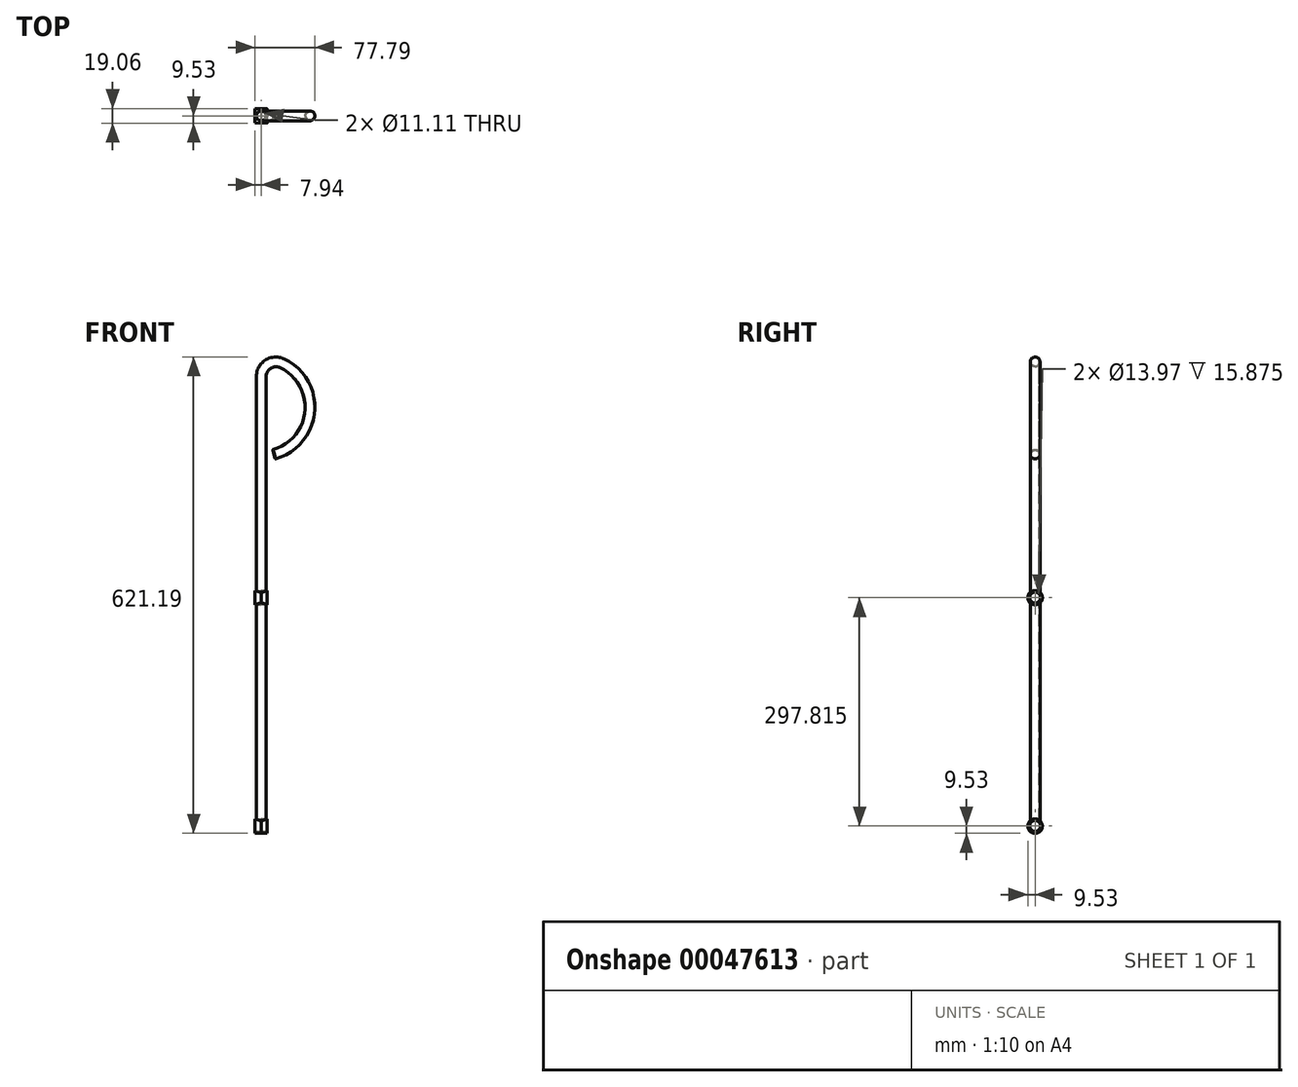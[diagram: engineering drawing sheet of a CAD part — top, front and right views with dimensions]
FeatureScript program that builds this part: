
annotation { "Feature Type Name" : "Feature", "Feature Type Description" : "" }
export const myFeature = defineFeature(function(context is Context, id is Id, definition is map)
    precondition{}
    {
        {
            var Q0;
            Q0=qCreatedBy(makeId("Front.planeOp"),FACE);
            var sketch = newSketch(context, id + "F0", { "sketchPlane" : qUnion([Q0])});
            skLineSegment(sketch, "E0", {"start": v(0, 0) * mm, "end": v(0, 586.26) * mm});
            skArc(sketch, "E1", {"start": v(16.44, 484.76) * mm, "mid": v(63.24, 540.36) * mm, "end": v(27.21, 603.47) * mm});
            skLineSegment(sketch, "E2", {"start": v(0, 546.1) * mm, "end": v(30.83, 431.05) * mm, "construction": true});
            skPoint(sketch, "E3.visualSharp", {"position": v(0, 609.6) * mm});
            skArc(sketch, "E3.filletArc", {"start": v(27.21, 603.47) * mm, "mid": v(8.87, 602.36) * mm, "end": v(0, 586.26) * mm});
            skSolve(sketch);
        }
        {
            var Q0;
            Q0=qCreatedBy(makeId("Top.planeOp"),FACE);
            var sketch = newSketch(context, id + "F1", { "sketchPlane" : qUnion([Q0])});
            skCircle(sketch, "E4", {"center": v(0, 0) * mm, "radius": 6.35 * mm});
            skCircle(sketch, "E5", {"center": v(0, 0) * mm, "radius": 5.56 * mm});
            skSolve(sketch);
        }
        {
            var Q0;
            Q0=qSketchRegion(id+"F1",true);
            var Q1;
            Q1=qConstructionFilter(qBodyType(qCreatedBy(id+"F0",EDGE),BodyType.WIRE),ConstructionObject.NO);
            sweep(context, id + "F2", {"profiles" : qUnion([Q0]), "path" : qUnion([Q1])});
        }
        {
            var Q0;
            Q0=makeQuery(id+"F2.opSweep","CAP_EDGE",EDGE,{"disambiguationData":[OSD([sQuery(id+"F0.wireOp",VERTEX,"E1.start"),sQuery(id+"F1.wireOp",EDGE,"E4")])],"isStart":false});
            chamfer(context, id + "F3", {"entities" : qUnion([Q0]), "width" : 0.8 * mm, "tangentPropagation" : true});
        }
        {
            var Q0;
            Q0=qCreatedBy(makeId("Right.planeOp"),FACE);
            var sketch = newSketch(context, id + "F4", { "sketchPlane" : qUnion([Q0])});
            skCircle(sketch, "E6", {"center": v(0, 0) * mm, "radius": 9.53 * mm});
            skSolve(sketch);
        }
        {
            var Q0;
            Q0=qSketchRegion(id+"F4",true);
            extrude(context, id + "F5", {"entities" : qUnion([Q0]), "operationType" : NewBodyOperationType.ADD, "depth" : 15.88 * mm, "hasDraft" : true, "draftAngle" : 3 * degree, "draftPullDirection" : true, "symmetric" : true});
        }
        {
            var Q0;
            Q0=makeQuery(id+"F5.opExtrude","CAP_FACE",FACE,{"disambiguationData":[OSD([sQuery(id+"F4.wireOp",EDGE,"E6")])],"isStart":false});
            var sketch = newSketch(context, id + "F6", { "sketchPlane" : qUnion([Q0])});
            skCircle(sketch, "E7", {"center": v(0, 0) * mm, "radius": 6.99 * mm});
            skSolve(sketch);
        }
        {
            var Q0;
            Q0=qSketchRegion(id+"F6",true);
            var Q1;
            Q1=makeQuery(id+"F5.opExtrude","CAP_FACE",FACE,{"disambiguationData":[OSD([sQuery(id+"F4.wireOp",EDGE,"E6")])],"isStart":true});
            extrude(context, id + "F7", {"entities" : qUnion([Q0]), "operationType" : NewBodyOperationType.REMOVE, "endBound" : BoundingType.UP_TO_SURFACE, "oppositeDirection" : true, "endBoundEntityFace" : qUnion([Q1]), "depth" : 25.4 * mm});
        }
        {
            var Q0;
            Q0=qCreatedBy(makeId("Right.planeOp"),FACE);
            var sketch = newSketch(context, id + "F8", { "sketchPlane" : qUnion([Q0])});
            skCircle(sketch, "E8", {"center": v(0, 297.81) * mm, "radius": 9.53 * mm});
            skSolve(sketch);
        }
        {
            var Q0;
            Q0=qSketchRegion(id+"F8",true);
            extrude(context, id + "F9", {"entities" : qUnion([Q0]), "operationType" : NewBodyOperationType.ADD, "depth" : 15.88 * mm, "hasDraft" : true, "draftAngle" : 3 * degree, "draftPullDirection" : true, "symmetric" : true});
        }
        {
            var Q0;
            Q0=makeQuery(id+"F9.opExtrude","CAP_FACE",FACE,{"disambiguationData":[OSD([sQuery(id+"F8.wireOp",EDGE,"E8")])],"isStart":false});
            var sketch = newSketch(context, id + "F10", { "sketchPlane" : qUnion([Q0])});
            skCircle(sketch, "E9", {"center": v(0, 297.81) * mm, "radius": 6.99 * mm});
            skSolve(sketch);
        }
        {
            var Q0;
            Q0=qSketchRegion(id+"F10",true);
            var Q1;
            Q1=makeQuery(id+"F9.opExtrude","CAP_FACE",FACE,{"disambiguationData":[OSD([sQuery(id+"F8.wireOp",EDGE,"E8")])],"isStart":true});
            extrude(context, id + "F11", {"entities" : qUnion([Q0]), "operationType" : NewBodyOperationType.REMOVE, "endBound" : BoundingType.UP_TO_SURFACE, "oppositeDirection" : true, "endBoundEntityFace" : qUnion([Q1]), "depth" : 25.4 * mm});
        }
    });
